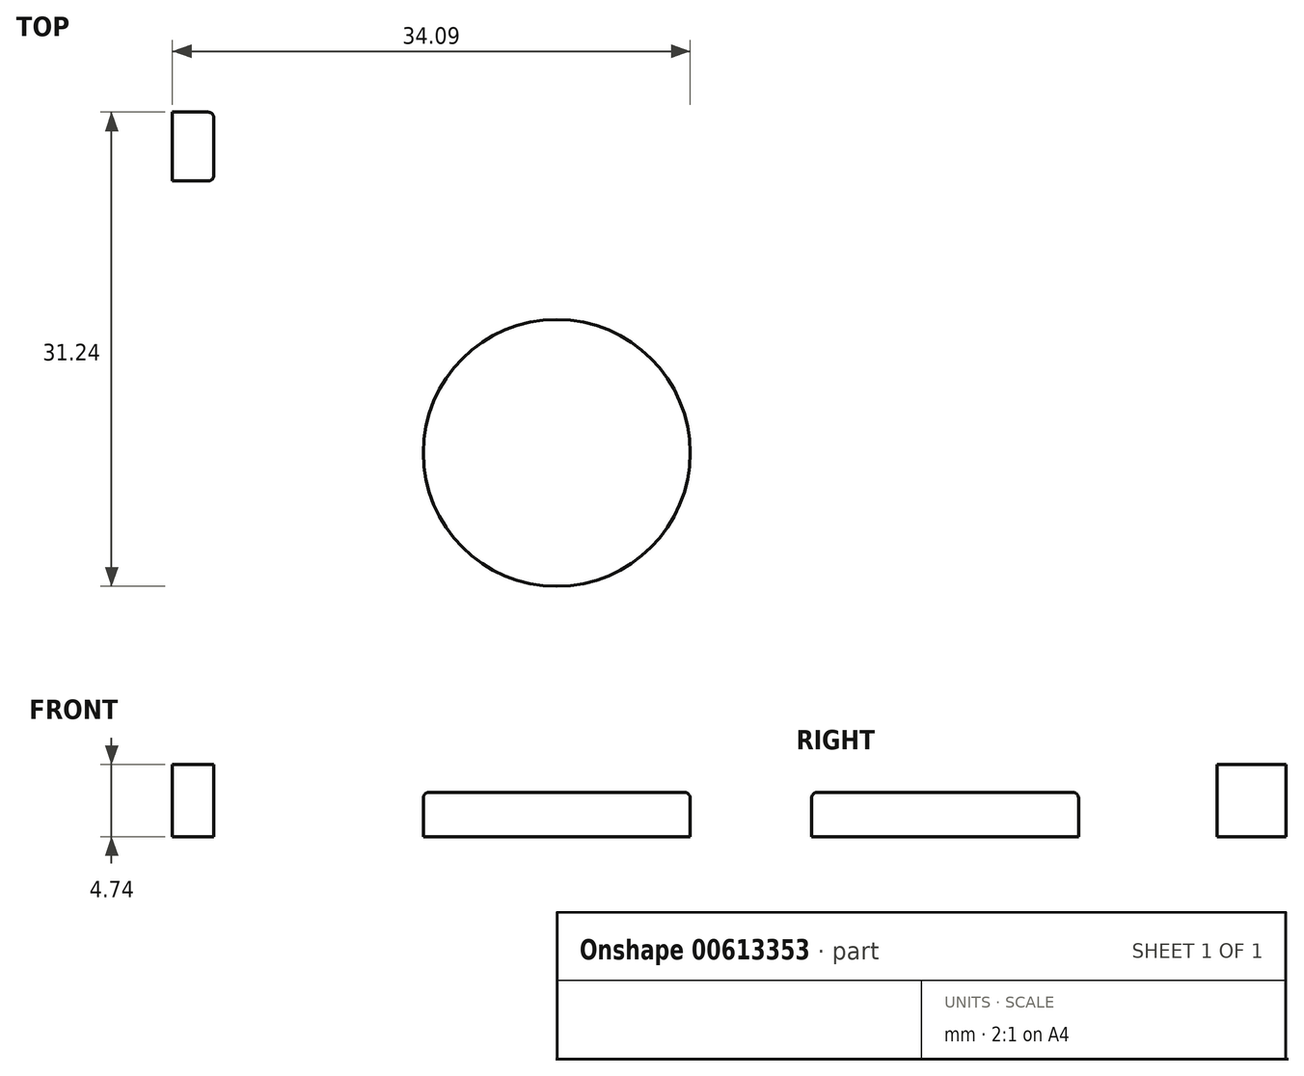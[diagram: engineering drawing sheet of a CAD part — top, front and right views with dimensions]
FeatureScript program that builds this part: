
annotation { "Feature Type Name" : "Feature", "Feature Type Description" : "" }
export const myFeature = defineFeature(function(context is Context, id is Id, definition is map)
    precondition{}
    {
        {
            var Q0;
            Q0=qCreatedBy(makeId("Top.planeOp"),FACE);
            var sketch = newSketch(context, id + "F0", { "sketchPlane" : qUnion([Q0])});
            skLineSegment(sketch, "E0.bottom", {"start": v(-25.25, 15.65) * mm, "end": v(-7.85, 15.65) * mm});
            skLineSegment(sketch, "E0.top", {"start": v(-25.25, -18.56) * mm, "end": v(-7.85, -18.56) * mm});
            skLineSegment(sketch, "E0.left", {"start": v(-25.25, 15.65) * mm, "end": v(-25.25, -18.56) * mm});
            skLineSegment(sketch, "E0.right", {"start": v(-7.85, 15.65) * mm, "end": v(-7.85, -18.56) * mm});
            skLineSegment(sketch, "E1.bottom", {"start": v(-7.85, 15.65) * mm, "end": v(-10.58, 15.65) * mm});
            skLineSegment(sketch, "E1.top", {"start": v(-7.85, 11.1) * mm, "end": v(-10.58, 11.1) * mm});
            skLineSegment(sketch, "E1.left", {"start": v(-7.85, 15.65) * mm, "end": v(-7.85, 11.1) * mm});
            skLineSegment(sketch, "E1.right", {"start": v(-10.58, 15.65) * mm, "end": v(-10.58, 11.1) * mm});
            skLineSegment(sketch, "E2", {"start": v(-7.85, -1.46) * mm, "end": v(-25.25, -1.46) * mm, "construction": true});
            skLineSegment(sketch, "E3.MirrorCS", {"start": v(-10.58, -18.56) * mm, "end": v(-10.58, -14.02) * mm});
            skLineSegment(sketch, "E4.MirrorCS", {"start": v(-7.85, -14.02) * mm, "end": v(-10.58, -14.02) * mm});
            skCircle(sketch, "E5", {"center": v(14.72, -6.8) * mm, "radius": 8.79 * mm});
            skSolve(sketch);
        }
        {
            var Q0;
            Q0=makeQuery(id+"F0.imprint","IMPRINT",FACE,{"disambiguationData":[TD([[makeQuery(id+"F0.imprint","IMPRINT",EDGE,{"derivedFrom":sQuery(id+"F0.wireOp",EDGE,"E0.bottom")}),-1.0]])]});
            extrude(context, id + "F1", {"entities" : qUnion([Q0]), "depth" : 4.74 * mm, "offsetDistance" : 25 * mm});
        }
        {
            var Q0;
            Q0=makeQuery(id+"F0.imprint","IMPRINT",FACE,{"disambiguationData":[TD([[makeQuery(id+"F0.imprint","IMPRINT",EDGE,{"derivedFrom":sQuery(id+"F0.wireOp",EDGE,"E5")}),1.0]])]});
            extrude(context, id + "F2", {"entities" : qUnion([Q0]), "depth" : 2.92 * mm, "offsetDistance" : 25 * mm});
        }
        {
            var Q0;
            Q0=makeQuery(id+"F1.opExtrude","SWEPT_EDGE",EDGE,{"disambiguationData":[OSD([sQuery(id+"F0.wireOp",EDGE,"E0.right"),sQuery(id+"F0.wireOp",EDGE,"E4.MirrorCS")])]});
            var Q1;
            Q1=makeQuery(id+"F1.opExtrude","SWEPT_EDGE",EDGE,{"disambiguationData":[OSD([sQuery(id+"F0.wireOp",EDGE,"E0.right"),sQuery(id+"F0.wireOp",EDGE,"E1.top"),sQuery(id+"F0.wireOp",EDGE,"E1.left")])]});
            var Q2;
            Q2=makeQuery(id+"F2.opExtrude","CAP_EDGE",EDGE,{"disambiguationData":[OSD([sQuery(id+"F0.wireOp",EDGE,"E5")])],"isStart":false});
            fillet(context, id + "F3", {"entities" : qUnion([Q0, Q1, Q2]), "radius" : 0.4 * mm, "tangentPropagation" : true, "allowEdgeOverflow" : false});
        }
    });
